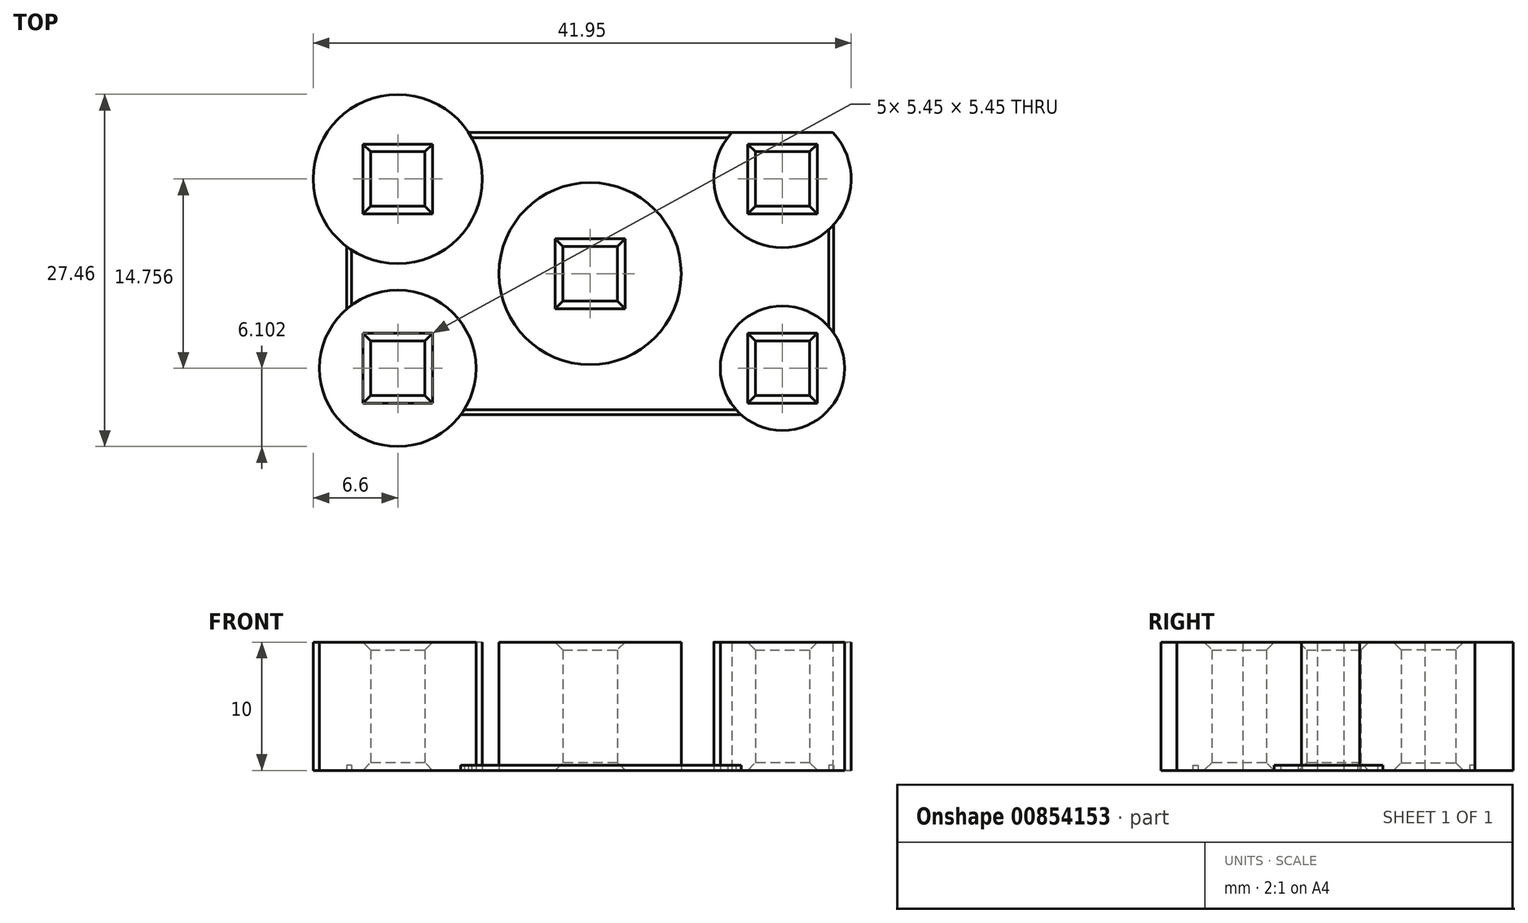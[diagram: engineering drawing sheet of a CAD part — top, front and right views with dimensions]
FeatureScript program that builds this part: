
annotation { "Feature Type Name" : "Feature", "Feature Type Description" : "" }
export const myFeature = defineFeature(function(context is Context, id is Id, definition is map)
    precondition{}
    {
        {
            var Q0;
            Q0=qCreatedBy(makeId("Top.planeOp"),FACE);
            var sketch = newSketch(context, id + "F0", { "sketchPlane" : qUnion([Q0])});
            skLineSegment(sketch, "E0.bottom", {"start": v(15, -7.38) * mm, "end": v(-15, -7.38) * mm, "construction": true});
            skLineSegment(sketch, "E0.top", {"start": v(15, 7.38) * mm, "end": v(-15, 7.38) * mm, "construction": true});
            skLineSegment(sketch, "E0.left", {"start": v(15, -7.38) * mm, "end": v(15, 7.38) * mm, "construction": true});
            skLineSegment(sketch, "E0.right", {"start": v(-15, -7.38) * mm, "end": v(-15, 7.38) * mm, "construction": true});
            skPoint(sketch, "E0.middle", {"position": v(0, 0) * mm});
            skCircle(sketch, "E1", {"center": v(-15, 7.38) * mm, "radius": 6.6 * mm});
            skCircle(sketch, "E2", {"center": v(-15, -7.38) * mm, "radius": 6.1 * mm});
            skCircle(sketch, "E3", {"center": v(15, -7.38) * mm, "radius": 4.85 * mm});
            skCircle(sketch, "E4", {"center": v(15, 7.38) * mm, "radius": 5.35 * mm});
            skCircle(sketch, "E5", {"center": v(0, 0) * mm, "radius": 7.1 * mm});
            skLineSegment(sketch, "E6.bottom", {"start": v(-12.87, 5.25) * mm, "end": v(-17.12, 5.25) * mm});
            skLineSegment(sketch, "E6.top", {"start": v(-12.87, 9.5) * mm, "end": v(-17.12, 9.5) * mm});
            skLineSegment(sketch, "E6.left", {"start": v(-12.87, 5.25) * mm, "end": v(-12.87, 9.5) * mm});
            skLineSegment(sketch, "E6.right", {"start": v(-17.12, 5.25) * mm, "end": v(-17.12, 9.5) * mm});
            skLineSegment(sketch, "E7.bottom", {"start": v(-12.87, -9.5) * mm, "end": v(-17.13, -9.5) * mm});
            skLineSegment(sketch, "E7.top", {"start": v(-12.87, -5.25) * mm, "end": v(-17.13, -5.25) * mm});
            skLineSegment(sketch, "E7.left", {"start": v(-12.87, -9.5) * mm, "end": v(-12.87, -5.25) * mm});
            skLineSegment(sketch, "E7.right", {"start": v(-17.13, -9.5) * mm, "end": v(-17.13, -5.25) * mm});
            skLineSegment(sketch, "E8.bottom", {"start": v(2.13, -2.12) * mm, "end": v(-2.12, -2.13) * mm});
            skLineSegment(sketch, "E8.top", {"start": v(2.12, 2.13) * mm, "end": v(-2.13, 2.12) * mm});
            skLineSegment(sketch, "E8.left", {"start": v(2.13, -2.12) * mm, "end": v(2.12, 2.13) * mm});
            skLineSegment(sketch, "E8.right", {"start": v(-2.12, -2.13) * mm, "end": v(-2.13, 2.12) * mm});
            skLineSegment(sketch, "E9.left", {"start": v(17.02, 2.42) * mm, "end": v(17.02, 7.82) * mm});
            skLineSegment(sketch, "E10.bottom", {"start": v(17.13, -9.5) * mm, "end": v(12.88, -9.5) * mm});
            skLineSegment(sketch, "E10.top", {"start": v(17.13, -5.25) * mm, "end": v(12.88, -5.25) * mm});
            skLineSegment(sketch, "E10.left", {"start": v(17.13, -9.5) * mm, "end": v(17.13, -5.25) * mm});
            skLineSegment(sketch, "E10.right", {"start": v(12.88, -9.5) * mm, "end": v(12.88, -5.25) * mm});
            skLineSegment(sketch, "E11.bottom", {"start": v(17.13, 5.25) * mm, "end": v(12.88, 5.25) * mm});
            skLineSegment(sketch, "E11.top", {"start": v(17.13, 9.5) * mm, "end": v(12.88, 9.5) * mm});
            skLineSegment(sketch, "E11.left", {"start": v(17.13, 5.25) * mm, "end": v(17.13, 9.5) * mm});
            skLineSegment(sketch, "E11.right", {"start": v(12.88, 5.25) * mm, "end": v(12.88, 9.5) * mm});
            skLineSegment(sketch, "E12.bottom", {"start": v(19, -11) * mm, "end": v(-19, -11) * mm});
            skLineSegment(sketch, "E12.top", {"start": v(19, 11) * mm, "end": v(-19, 11) * mm});
            skLineSegment(sketch, "E12.left", {"start": v(19, -11) * mm, "end": v(19, 11) * mm});
            skLineSegment(sketch, "E12.right", {"start": v(-19, -11) * mm, "end": v(-19, 11) * mm});
            skLineSegment(sketch, "E13.bottom", {"start": v(18.6, -10.6) * mm, "end": v(-18.6, -10.6) * mm});
            skLineSegment(sketch, "E13.top", {"start": v(18.6, 10.6) * mm, "end": v(-18.6, 10.6) * mm});
            skLineSegment(sketch, "E13.left", {"start": v(18.6, -10.6) * mm, "end": v(18.6, 10.6) * mm});
            skLineSegment(sketch, "E13.right", {"start": v(-18.6, -10.6) * mm, "end": v(-18.6, 10.6) * mm});
            skSolve(sketch);
        }
        {
            var Q0;
            Q0=makeQuery(id+"F0.imprint","IMPRINT",FACE,{"disambiguationData":[TD([[makeQuery(id+"F0.imprint","IMPRINT",EDGE,{"derivedFrom":sQuery(id+"F0.wireOp",EDGE,"E3")}),1.0]])]});
            var Q1;
            Q1=makeQuery(id+"F0.imprint","IMPRINT",FACE,{"disambiguationData":[TD([[makeQuery(id+"F0.imprint","IMPRINT",EDGE,{"derivedFrom":sQuery(id+"F0.wireOp",EDGE,"E1")}),1.0]])]});
            var Q2;
            Q2=makeQuery(id+"F0.imprint","IMPRINT",FACE,{"disambiguationData":[TD([[makeQuery(id+"F0.imprint","IMPRINT",EDGE,{"derivedFrom":sQuery(id+"F0.wireOp",EDGE,"E2")}),1.0]])]});
            var Q3;
            Q3=makeQuery(id+"F0.imprint","IMPRINT",FACE,{"disambiguationData":[TD([[makeQuery(id+"F0.imprint","IMPRINT",EDGE,{"derivedFrom":sQuery(id+"F0.wireOp",EDGE,"E5")}),1.0]])]});
            var Q4;
            Q4=makeQuery(id+"F0.imprint","IMPRINT",FACE,{"disambiguationData":[TD([[makeQuery(id+"F0.imprint","IMPRINT",EDGE,{"derivedFrom":sQuery(id+"F0.wireOp",EDGE,"E4")}),1.0]])]});
            var Q5;
            {var subQ0=sQuery(id+"F0.wireOp",EDGE,"E12.top");var subQ1=sQuery(id+"F0.wireOp",EDGE,"E1");var subQ2=makeQuery(id+"F0.imprint","INTERSECT",VERTEX,{"derivedFrom":[subQ1,subQ0]});Q5=makeQuery(id+"F0.imprint","IMPRINT",FACE,{"disambiguationData":[TD([[makeQuery(id+"F0.imprint","IMPRINT",EDGE,{"disambiguationData":[TD([[subQ2,-1.0]])],"derivedFrom":subQ1}),1.0]])]});}
            var Q6;
            Q6=makeQuery(id+"F0.imprint","IMPRINT",FACE,{"disambiguationData":[TD([[makeQuery(id+"F0.imprint","IMPRINT",EDGE,{"derivedFrom":sQuery(id+"F0.wireOp",EDGE,"E6.bottom")}),1.0]])]});
            var Q7;
            Q7=makeQuery(id+"F0.imprint","IMPRINT",FACE,{"disambiguationData":[TD([[makeQuery(id+"F0.imprint","IMPRINT",EDGE,{"derivedFrom":sQuery(id+"F0.wireOp",EDGE,"E7.bottom")}),1.0]])]});
            var Q8;
            {var subQ0=sQuery(id+"F0.wireOp",EDGE,"E12.right");var subQ1=sQuery(id+"F0.wireOp",EDGE,"E2");var subQ2=makeQuery(id+"F0.imprint","INTERSECT",VERTEX,{"derivedFrom":[subQ1,subQ0]});Q8=makeQuery(id+"F0.imprint","IMPRINT",FACE,{"disambiguationData":[TD([[makeQuery(id+"F0.imprint","IMPRINT",EDGE,{"disambiguationData":[TD([[subQ2,-1.0]])],"derivedFrom":subQ1}),1.0]])]});}
            var Q9;
            {var subQ0=sQuery(id+"F0.wireOp",EDGE,"E12.bottom");var subQ1=sQuery(id+"F0.wireOp",EDGE,"E3");var subQ2=makeQuery(id+"F0.imprint","INTERSECT",VERTEX,{"disambiguationData":[OD(0.0)],"derivedFrom":[subQ1,subQ0]});Q9=makeQuery(id+"F0.imprint","IMPRINT",FACE,{"disambiguationData":[TD([[makeQuery(id+"F0.imprint","IMPRINT",EDGE,{"disambiguationData":[TD([[subQ2,-1.0]])],"derivedFrom":subQ1}),1.0]])]});}
            var Q10;
            {var subQ0=sQuery(id+"F0.wireOp",EDGE,"E12.left");var subQ1=sQuery(id+"F0.wireOp",EDGE,"E3");var subQ2=makeQuery(id+"F0.imprint","INTERSECT",VERTEX,{"disambiguationData":[OD(0.0)],"derivedFrom":[subQ1,subQ0]});Q10=makeQuery(id+"F0.imprint","IMPRINT",FACE,{"disambiguationData":[TD([[makeQuery(id+"F0.imprint","IMPRINT",EDGE,{"disambiguationData":[TD([[subQ2,1.0]])],"derivedFrom":subQ1}),1.0]])]});}
            var Q11;
            Q11=makeQuery(id+"F0.imprint","IMPRINT",FACE,{"disambiguationData":[TD([[makeQuery(id+"F0.imprint","IMPRINT",EDGE,{"derivedFrom":sQuery(id+"F0.wireOp",EDGE,"E10.bottom")}),1.0]])]});
            var Q12;
            {var subQ0=sQuery(id+"F0.wireOp",EDGE,"E12.left");var subQ1=sQuery(id+"F0.wireOp",EDGE,"E4");var subQ2=makeQuery(id+"F0.imprint","INTERSECT",VERTEX,{"disambiguationData":[OD(0.0)],"derivedFrom":[subQ1,subQ0]});Q12=makeQuery(id+"F0.imprint","IMPRINT",FACE,{"disambiguationData":[TD([[makeQuery(id+"F0.imprint","IMPRINT",EDGE,{"disambiguationData":[TD([[subQ2,1.0]])],"derivedFrom":subQ1}),1.0]])]});}
            var Q13;
            {var subQ0=sQuery(id+"F0.wireOp",EDGE,"E12.top");var subQ1=sQuery(id+"F0.wireOp",EDGE,"E4");var subQ2=makeQuery(id+"F0.imprint","INTERSECT",VERTEX,{"disambiguationData":[OD(0.0)],"derivedFrom":[subQ1,subQ0]});Q13=makeQuery(id+"F0.imprint","IMPRINT",FACE,{"disambiguationData":[TD([[makeQuery(id+"F0.imprint","IMPRINT",EDGE,{"disambiguationData":[TD([[subQ2,-1.0]])],"derivedFrom":subQ1}),1.0]])]});}
            var Q14;
            Q14=makeQuery(id+"F0.imprint","IMPRINT",FACE,{"disambiguationData":[TD([[makeQuery(id+"F0.imprint","IMPRINT",EDGE,{"derivedFrom":sQuery(id+"F0.wireOp",EDGE,"E11.top")}),-1.0]])]});
            extrude(context, id + "F1", {"entities" : qUnion([Q0, Q1, Q2, Q3, Q4, Q5, Q6, Q7, Q8, Q9, Q10, Q11, Q12, Q13, Q14]), "depth" : 10 * mm, "offsetDistance" : 25 * mm});
        }
        {
            var Q0;
            Q0=makeQuery(id+"F1.opExtrude","CAP_EDGE",EDGE,{"disambiguationData":[OSD([sQuery(id+"F0.wireOp",EDGE,"E8.right")])],"isStart":false});
            var Q1;
            Q1=makeQuery(id+"F1.opExtrude","CAP_EDGE",EDGE,{"disambiguationData":[OSD([sQuery(id+"F0.wireOp",EDGE,"E8.bottom")])],"isStart":false});
            var Q2;
            Q2=makeQuery(id+"F1.opExtrude","CAP_EDGE",EDGE,{"disambiguationData":[OSD([sQuery(id+"F0.wireOp",EDGE,"E8.top")])],"isStart":false});
            var Q3;
            Q3=makeQuery(id+"F1.opExtrude","CAP_EDGE",EDGE,{"disambiguationData":[OSD([sQuery(id+"F0.wireOp",EDGE,"E8.left")])],"isStart":false});
            var Q4;
            Q4=makeQuery(id+"F1.opExtrude","CAP_EDGE",EDGE,{"disambiguationData":[OSD([sQuery(id+"F0.wireOp",EDGE,"E10.right")])],"isStart":false});
            var Q5;
            Q5=makeQuery(id+"F1.opExtrude","CAP_EDGE",EDGE,{"disambiguationData":[OSD([sQuery(id+"F0.wireOp",EDGE,"E10.top")])],"isStart":false});
            var Q6;
            Q6=makeQuery(id+"F1.opExtrude","CAP_EDGE",EDGE,{"disambiguationData":[OSD([sQuery(id+"F0.wireOp",EDGE,"E10.left")])],"isStart":false});
            var Q7;
            Q7=makeQuery(id+"F1.opExtrude","CAP_EDGE",EDGE,{"disambiguationData":[OSD([sQuery(id+"F0.wireOp",EDGE,"E10.bottom")])],"isStart":false});
            var Q8;
            Q8=makeQuery(id+"F1.opExtrude","CAP_EDGE",EDGE,{"disambiguationData":[OSD([sQuery(id+"F0.wireOp",EDGE,"E11.right")])],"isStart":false});
            var Q9;
            Q9=makeQuery(id+"F1.opExtrude","CAP_EDGE",EDGE,{"disambiguationData":[OSD([sQuery(id+"F0.wireOp",EDGE,"E11.top")])],"isStart":false});
            var Q10;
            Q10=makeQuery(id+"F1.opExtrude","CAP_EDGE",EDGE,{"disambiguationData":[OSD([sQuery(id+"F0.wireOp",EDGE,"E11.bottom")])],"isStart":false});
            var Q11;
            Q11=makeQuery(id+"F1.opExtrude","CAP_EDGE",EDGE,{"disambiguationData":[OSD([sQuery(id+"F0.wireOp",EDGE,"E11.left")])],"isStart":false});
            var Q12;
            Q12=makeQuery(id+"F1.opExtrude","CAP_EDGE",EDGE,{"disambiguationData":[OSD([sQuery(id+"F0.wireOp",EDGE,"E7.right")])],"isStart":false});
            var Q13;
            Q13=makeQuery(id+"F1.opExtrude","CAP_EDGE",EDGE,{"disambiguationData":[OSD([sQuery(id+"F0.wireOp",EDGE,"E7.bottom")])],"isStart":false});
            var Q14;
            Q14=makeQuery(id+"F1.opExtrude","CAP_EDGE",EDGE,{"disambiguationData":[OSD([sQuery(id+"F0.wireOp",EDGE,"E7.top")])],"isStart":false});
            var Q15;
            Q15=makeQuery(id+"F1.opExtrude","CAP_EDGE",EDGE,{"disambiguationData":[OSD([sQuery(id+"F0.wireOp",EDGE,"E7.left")])],"isStart":false});
            var Q16;
            Q16=makeQuery(id+"F1.opExtrude","CAP_EDGE",EDGE,{"disambiguationData":[OSD([sQuery(id+"F0.wireOp",EDGE,"E6.right")])],"isStart":false});
            var Q17;
            Q17=makeQuery(id+"F1.opExtrude","CAP_EDGE",EDGE,{"disambiguationData":[OSD([sQuery(id+"F0.wireOp",EDGE,"E6.bottom")])],"isStart":false});
            var Q18;
            Q18=makeQuery(id+"F1.opExtrude","CAP_EDGE",EDGE,{"disambiguationData":[OSD([sQuery(id+"F0.wireOp",EDGE,"E6.left")])],"isStart":false});
            var Q19;
            Q19=makeQuery(id+"F1.opExtrude","CAP_EDGE",EDGE,{"disambiguationData":[OSD([sQuery(id+"F0.wireOp",EDGE,"E6.top")])],"isStart":false});
            chamfer(context, id + "F2", {"entities" : qUnion([Q0, Q1, Q2, Q3, Q4, Q5, Q6, Q7, Q8, Q9, Q10, Q11, Q12, Q13, Q14, Q15, Q16, Q17, Q18, Q19]), "width" : .6 * mm, "tangentPropagation" : true});
        }
        {
            var Q0;
            Q0=makeQuery(id+"F1.opExtrude","CAP_EDGE",EDGE,{"disambiguationData":[OSD([sQuery(id+"F0.wireOp",EDGE,"E6.bottom")])],"isStart":true});
            var Q1;
            Q1=makeQuery(id+"F1.opExtrude","CAP_EDGE",EDGE,{"disambiguationData":[OSD([sQuery(id+"F0.wireOp",EDGE,"E6.right")])],"isStart":true});
            var Q2;
            Q2=makeQuery(id+"F1.opExtrude","CAP_EDGE",EDGE,{"disambiguationData":[OSD([sQuery(id+"F0.wireOp",EDGE,"E6.top")])],"isStart":true});
            var Q3;
            Q3=makeQuery(id+"F1.opExtrude","CAP_EDGE",EDGE,{"disambiguationData":[OSD([sQuery(id+"F0.wireOp",EDGE,"E6.left")])],"isStart":true});
            var Q4;
            Q4=makeQuery(id+"F1.opExtrude","CAP_EDGE",EDGE,{"disambiguationData":[OSD([sQuery(id+"F0.wireOp",EDGE,"E7.right")])],"isStart":true});
            var Q5;
            Q5=makeQuery(id+"F1.opExtrude","CAP_EDGE",EDGE,{"disambiguationData":[OSD([sQuery(id+"F0.wireOp",EDGE,"E7.bottom")])],"isStart":true});
            var Q6;
            Q6=makeQuery(id+"F1.opExtrude","CAP_EDGE",EDGE,{"disambiguationData":[OSD([sQuery(id+"F0.wireOp",EDGE,"E7.left")])],"isStart":true});
            var Q7;
            Q7=makeQuery(id+"F1.opExtrude","CAP_EDGE",EDGE,{"disambiguationData":[OSD([sQuery(id+"F0.wireOp",EDGE,"E7.top")])],"isStart":true});
            var Q8;
            Q8=makeQuery(id+"F1.opExtrude","CAP_EDGE",EDGE,{"disambiguationData":[OSD([sQuery(id+"F0.wireOp",EDGE,"E8.right")])],"isStart":true});
            var Q9;
            Q9=makeQuery(id+"F1.opExtrude","CAP_EDGE",EDGE,{"disambiguationData":[OSD([sQuery(id+"F0.wireOp",EDGE,"E8.bottom")])],"isStart":true});
            var Q10;
            Q10=makeQuery(id+"F1.opExtrude","CAP_EDGE",EDGE,{"disambiguationData":[OSD([sQuery(id+"F0.wireOp",EDGE,"E8.left")])],"isStart":true});
            var Q11;
            Q11=makeQuery(id+"F1.opExtrude","CAP_EDGE",EDGE,{"disambiguationData":[OSD([sQuery(id+"F0.wireOp",EDGE,"E8.top")])],"isStart":true});
            var Q12;
            Q12=makeQuery(id+"F1.opExtrude","CAP_EDGE",EDGE,{"disambiguationData":[OSD([sQuery(id+"F0.wireOp",EDGE,"E11.right")])],"isStart":true});
            var Q13;
            Q13=makeQuery(id+"F1.opExtrude","CAP_EDGE",EDGE,{"disambiguationData":[OSD([sQuery(id+"F0.wireOp",EDGE,"E11.bottom")])],"isStart":true});
            var Q14;
            Q14=makeQuery(id+"F1.opExtrude","CAP_EDGE",EDGE,{"disambiguationData":[OSD([sQuery(id+"F0.wireOp",EDGE,"E11.left")])],"isStart":true});
            var Q15;
            Q15=makeQuery(id+"F1.opExtrude","CAP_EDGE",EDGE,{"disambiguationData":[OSD([sQuery(id+"F0.wireOp",EDGE,"E11.top")])],"isStart":true});
            var Q16;
            Q16=makeQuery(id+"F1.opExtrude","CAP_EDGE",EDGE,{"disambiguationData":[OSD([sQuery(id+"F0.wireOp",EDGE,"E10.right")])],"isStart":true});
            var Q17;
            Q17=makeQuery(id+"F1.opExtrude","CAP_EDGE",EDGE,{"disambiguationData":[OSD([sQuery(id+"F0.wireOp",EDGE,"E10.bottom")])],"isStart":true});
            var Q18;
            Q18=makeQuery(id+"F1.opExtrude","CAP_EDGE",EDGE,{"disambiguationData":[OSD([sQuery(id+"F0.wireOp",EDGE,"E10.left")])],"isStart":true});
            var Q19;
            Q19=makeQuery(id+"F1.opExtrude","CAP_EDGE",EDGE,{"disambiguationData":[OSD([sQuery(id+"F0.wireOp",EDGE,"E10.top")])],"isStart":true});
            chamfer(context, id + "F3", {"entities" : qUnion([Q0, Q1, Q2, Q3, Q4, Q5, Q6, Q7, Q8, Q9, Q10, Q11, Q12, Q13, Q14, Q15, Q16, Q17, Q18, Q19]), "width" : .6 * mm, "tangentPropagation" : true});
        }
        {
            var Q0;
            {var subQ0=sQuery(id+"F0.wireOp",EDGE,"E12.right");var subQ1=sQuery(id+"F0.wireOp",EDGE,"E1");var subQ2=makeQuery(id+"F0.imprint","INTERSECT",VERTEX,{"derivedFrom":[subQ1,subQ0]});Q0=makeQuery(id+"F0.imprint","IMPRINT",FACE,{"disambiguationData":[TD([[makeQuery(id+"F0.imprint","IMPRINT",EDGE,{"disambiguationData":[TD([[subQ2,-1.0]])],"derivedFrom":subQ1}),-1.0]])]});}
            var Q1;
            {var subQ0=sQuery(id+"F0.wireOp",EDGE,"E12.bottom");var subQ1=sQuery(id+"F0.wireOp",EDGE,"E2");var subQ2=makeQuery(id+"F0.imprint","INTERSECT",VERTEX,{"derivedFrom":[subQ1,subQ0]});Q1=makeQuery(id+"F0.imprint","IMPRINT",FACE,{"disambiguationData":[TD([[makeQuery(id+"F0.imprint","IMPRINT",EDGE,{"disambiguationData":[TD([[subQ2,-1.0]])],"derivedFrom":subQ1}),-1.0]])]});}
            var Q2;
            {var subQ0=sQuery(id+"F0.wireOp",EDGE,"E12.left");var subQ1=sQuery(id+"F0.wireOp",EDGE,"E3");var subQ2=makeQuery(id+"F0.imprint","INTERSECT",VERTEX,{"disambiguationData":[OD(0.0)],"derivedFrom":[subQ1,subQ0]});Q2=makeQuery(id+"F0.imprint","IMPRINT",FACE,{"disambiguationData":[TD([[makeQuery(id+"F0.imprint","IMPRINT",EDGE,{"disambiguationData":[TD([[subQ2,-1.0]])],"derivedFrom":subQ1}),-1.0]])]});}
            var Q3;
            {var subQ0=sQuery(id+"F0.wireOp",EDGE,"E12.top");var subQ1=sQuery(id+"F0.wireOp",EDGE,"E1");var subQ2=makeQuery(id+"F0.imprint","INTERSECT",VERTEX,{"derivedFrom":[subQ1,subQ0]});Q3=makeQuery(id+"F0.imprint","IMPRINT",FACE,{"disambiguationData":[TD([[makeQuery(id+"F0.imprint","IMPRINT",EDGE,{"disambiguationData":[TD([[subQ2,1.0]])],"derivedFrom":subQ1}),-1.0]])]});}
            extrude(context, id + "F4", {"entities" : qUnion([Q0, Q1, Q2, Q3]), "depth" : .4 * mm, "offsetDistance" : 25 * mm});
        }
    });
